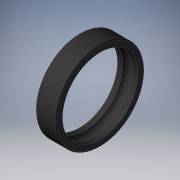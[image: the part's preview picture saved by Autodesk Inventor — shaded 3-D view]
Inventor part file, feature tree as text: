
AUTODESK INVENTOR PART (.ipt)
format: ipt  version: 2019 (Build 230136000, 136)  size: 186,880 bytes
history: native  units: mm
features: other x84, revolve x1, sketch x1
ambient origin geometry x8: Origin, YZ Plane, XZ Plane, XY Plane, X Axis, Y Axis, Z Axis, Center Point
bodies: Solid1 (feature_tree)
feature tree (86):
  revolve  "Revolution1"  [1 undecoded]
  other  "dgbb_or_XY"
  other  "dgbb_or_YZ"
  other  "dgbb_or_ZX"
  other  "dgbb_or_X"
  other  "dgbb_or_Y"
  other  "dgbb_or_Z"
  other  "dgbb_or_Center"
  other  "dgbb_or1_XY"
  other  "dgbb_or1_YZ"
  other  "dgbb_or1_ZX"
  other  "dgbb_or1_X"
  other  "dgbb_or1_Y"
  other  "dgbb_or1_Z"
  other  "dgbb_or1_Center"
  other  "dgbb_or11_1_XY"
  other  "dgbb_or11_1_YZ"
  other  "dgbb_or11_1_ZX"
  other  "dgbb_or11_1_X"
  other  "dgbb_or11_1_Y"
  other  "dgbb_or11_1_Z"
  other  "dgbb_or11_1_Center"
  other  "dgbb_or11_10_XY"
  other  "dgbb_or11_10_YZ"
  other  "dgbb_or11_10_ZX"
  other  "dgbb_or11_10_X"
  other  "dgbb_or11_10_Y"
  other  "dgbb_or11_10_Z"
  other  "dgbb_or11_10_Center"
  other  "dgbb_or11_2_XY"
  other  "dgbb_or11_2_YZ"
  other  "dgbb_or11_2_ZX"
  other  "dgbb_or11_2_X"
  other  "dgbb_or11_2_Y"
  other  "dgbb_or11_2_Z"
  other  "dgbb_or11_2_Center"
  other  "dgbb_or11_3_XY"
  other  "dgbb_or11_3_YZ"
  other  "dgbb_or11_3_ZX"
  other  "dgbb_or11_3_X"
  other  "dgbb_or11_3_Y"
  other  "dgbb_or11_3_Z"
  other  "dgbb_or11_3_Center"
  other  "dgbb_or11_4_XY"
  other  "dgbb_or11_4_YZ"
  other  "dgbb_or11_4_ZX"
  other  "dgbb_or11_4_X"
  other  "dgbb_or11_4_Y"
  other  "dgbb_or11_4_Z"
  other  "dgbb_or11_4_Center"
  other  "dgbb_or11_5_XY"
  other  "dgbb_or11_5_YZ"
  other  "dgbb_or11_5_ZX"
  other  "dgbb_or11_5_X"
  other  "dgbb_or11_5_Y"
  other  "dgbb_or11_5_Z"
  other  "dgbb_or11_5_Center"
  other  "dgbb_or11_6_XY"
  other  "dgbb_or11_6_YZ"
  other  "dgbb_or11_6_ZX"
  other  "dgbb_or11_6_X"
  other  "dgbb_or11_6_Y"
  other  "dgbb_or11_6_Z"
  other  "dgbb_or11_6_Center"
  other  "dgbb_or11_7_XY"
  other  "dgbb_or11_7_YZ"
  other  "dgbb_or11_7_ZX"
  other  "dgbb_or11_7_X"
  other  "dgbb_or11_7_Y"
  other  "dgbb_or11_7_Z"
  other  "dgbb_or11_7_Center"
  other  "dgbb_or11_8_XY"
  other  "dgbb_or11_8_YZ"
  other  "dgbb_or11_8_ZX"
  other  "dgbb_or11_8_X"
  other  "dgbb_or11_8_Y"
  other  "dgbb_or11_8_Z"
  other  "dgbb_or11_8_Center"
  other  "dgbb_or11_9_XY"
  other  "dgbb_or11_9_YZ"
  other  "dgbb_or11_9_ZX"
  other  "dgbb_or11_9_X"
  other  "dgbb_or11_9_Y"
  other  "dgbb_or11_9_Z"
  other  "dgbb_or11_9_Center"
  sketch  "Sketch_1"  dims[d0=360.0deg d1=0.0mm d2=0.0mm]
note: 1 required parameter value undecoded (feature->parameter linkage not recoverable at this tier; creation-order binding heuristic only, values carry confidence <= 0.55)
